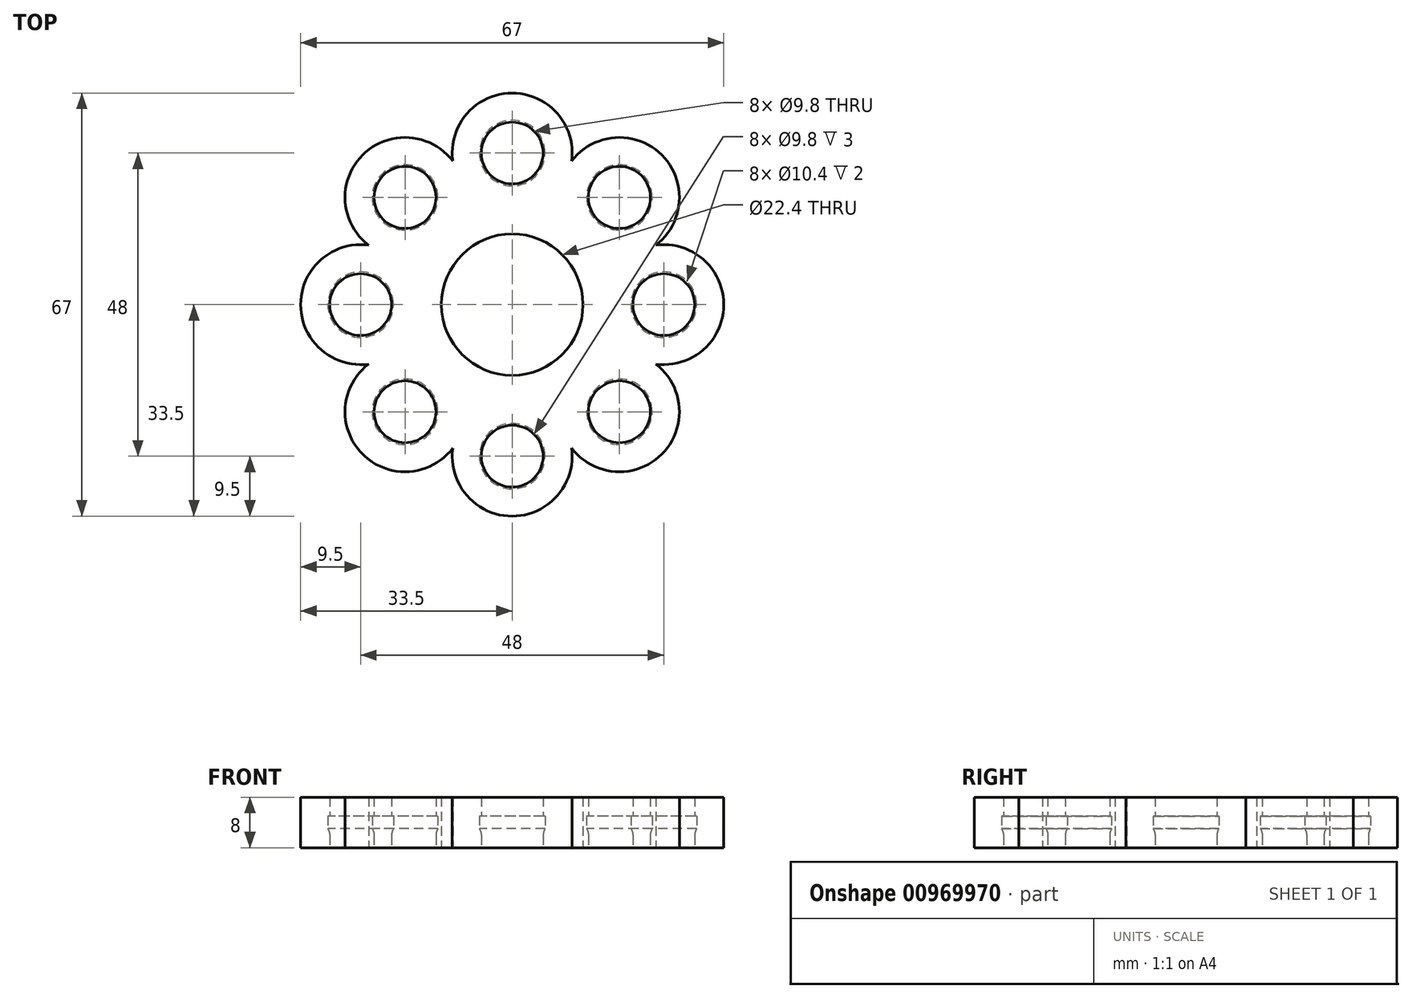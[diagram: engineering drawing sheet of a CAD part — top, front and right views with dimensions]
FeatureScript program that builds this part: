
annotation { "Feature Type Name" : "Feature", "Feature Type Description" : "" }
export const myFeature = defineFeature(function(context is Context, id is Id, definition is map)
    precondition{}
    {
        {
            var Q0;
            Q0=qCreatedBy(makeId("Top.planeOp"),FACE);
            var sketch = newSketch(context, id + "F0", { "sketchPlane" : qUnion([Q0])});
            skCircle(sketch, "E0", {"center": v(0, 0) * mm, "radius": 11.2 * mm});
            skCircle(sketch, "E1", {"center": v(0, 0) * mm, "radius": 24 * mm});
            skCircle(sketch, "E2", {"center": v(-24, 0) * mm, "radius": 5.2 * mm});
            skCircle(sketch, "E3", {"center": v(-24, 0) * mm, "radius": 9.5 * mm});
            skCircle(sketch, "E4", {"center": v(-24, 0) * mm, "radius": 4.9 * mm});
            skCircle(sketch, "E5.1.0", {"center": v(-16.97, -16.97) * mm, "radius": 4.9 * mm});
            skCircle(sketch, "E5.1.1", {"center": v(-16.97, -16.97) * mm, "radius": 5.2 * mm});
            skCircle(sketch, "E5.1.2", {"center": v(-16.97, -16.97) * mm, "radius": 9.5 * mm});
            skCircle(sketch, "E5.2.0", {"center": v(0, -24) * mm, "radius": 4.9 * mm});
            skCircle(sketch, "E5.2.1", {"center": v(0, -24) * mm, "radius": 5.2 * mm});
            skCircle(sketch, "E5.2.2", {"center": v(0, -24) * mm, "radius": 9.5 * mm});
            skCircle(sketch, "E5.3.0", {"center": v(16.97, -16.97) * mm, "radius": 4.9 * mm});
            skCircle(sketch, "E5.3.1", {"center": v(16.97, -16.97) * mm, "radius": 5.2 * mm});
            skCircle(sketch, "E5.3.2", {"center": v(16.97, -16.97) * mm, "radius": 9.5 * mm});
            skCircle(sketch, "E5.4.0", {"center": v(24, 0) * mm, "radius": 4.9 * mm});
            skCircle(sketch, "E5.4.1", {"center": v(24, 0) * mm, "radius": 5.2 * mm});
            skCircle(sketch, "E5.4.2", {"center": v(24, 0) * mm, "radius": 9.5 * mm});
            skCircle(sketch, "E5.5.0", {"center": v(16.97, 16.97) * mm, "radius": 4.9 * mm});
            skCircle(sketch, "E5.5.1", {"center": v(16.97, 16.97) * mm, "radius": 5.2 * mm});
            skCircle(sketch, "E5.5.2", {"center": v(16.97, 16.97) * mm, "radius": 9.5 * mm});
            skCircle(sketch, "E5.6.0", {"center": v(0, 24) * mm, "radius": 4.9 * mm});
            skCircle(sketch, "E5.6.1", {"center": v(0, 24) * mm, "radius": 5.2 * mm});
            skCircle(sketch, "E5.6.2", {"center": v(0, 24) * mm, "radius": 9.5 * mm});
            skCircle(sketch, "E5.7.0", {"center": v(-16.97, 16.97) * mm, "radius": 4.9 * mm});
            skCircle(sketch, "E5.7.1", {"center": v(-16.97, 16.97) * mm, "radius": 5.2 * mm});
            skCircle(sketch, "E5.7.2", {"center": v(-16.97, 16.97) * mm, "radius": 9.5 * mm});
            skSolve(sketch);
        }
        {
            var Q0;
            Q0=makeQuery(id+"F0.imprint","IMPRINT",FACE,{"disambiguationData":[TD([[makeQuery(id+"F0.imprint","IMPRINT",EDGE,{"derivedFrom":sQuery(id+"F0.wireOp",EDGE,"E0")}),-1.0]])]});
            var Q1;
            {var subQ0=sQuery(id+"F0.wireOp",EDGE,"E5.6.2");var subQ1=sQuery(id+"F0.wireOp",EDGE,"E1");var subQ2=makeQuery(id+"F0.imprint","INTERSECT",VERTEX,{"disambiguationData":[OD(1.0)],"derivedFrom":[subQ1,subQ0]});Q1=makeQuery(id+"F0.imprint","IMPRINT",FACE,{"disambiguationData":[TD([[makeQuery(id+"F0.imprint","IMPRINT",EDGE,{"disambiguationData":[TD([[subQ2,-1.0]])],"derivedFrom":subQ1}),1.0]])]});}
            var Q2;
            {var subQ1=sQuery(id+"F0.wireOp",EDGE,"E1");var subQ8=sQuery(id+"F0.wireOp",EDGE,"E5.5.2");var subQ9=makeQuery(id+"F0.imprint","INTERSECT",VERTEX,{"disambiguationData":[OD(1.0)],"derivedFrom":[subQ1,subQ8]});Q2=makeQuery(id+"F0.imprint","IMPRINT",FACE,{"disambiguationData":[TD([[makeQuery(id+"F0.imprint","IMPRINT",EDGE,{"disambiguationData":[TD([[subQ9,-1.0]])],"derivedFrom":subQ1}),1.0]])]});}
            var Q3;
            {var subQ1=sQuery(id+"F0.wireOp",EDGE,"E1");var subQ8=sQuery(id+"F0.wireOp",EDGE,"E5.4.2");var subQ9=makeQuery(id+"F0.imprint","INTERSECT",VERTEX,{"disambiguationData":[OD(0.0)],"derivedFrom":[subQ1,subQ8]});Q3=makeQuery(id+"F0.imprint","IMPRINT",FACE,{"disambiguationData":[TD([[makeQuery(id+"F0.imprint","IMPRINT",EDGE,{"disambiguationData":[TD([[subQ9,-1.0]])],"derivedFrom":subQ1}),1.0]])]});}
            var Q4;
            {var subQ1=sQuery(id+"F0.wireOp",EDGE,"E1");var subQ3=sQuery(id+"F0.wireOp",EDGE,"E5.4.1");var subQ5=makeQuery(id+"F0.imprint","INTERSECT",VERTEX,{"disambiguationData":[OD(0.0)],"derivedFrom":[subQ1,subQ3]});Q4=makeQuery(id+"F0.imprint","IMPRINT",FACE,{"disambiguationData":[TD([[makeQuery(id+"F0.imprint","IMPRINT",EDGE,{"disambiguationData":[TD([[subQ5,-1.0]])],"derivedFrom":subQ1}),1.0]])]});}
            var Q5;
            {var subQ1=sQuery(id+"F0.wireOp",EDGE,"E1");var subQ8=sQuery(id+"F0.wireOp",EDGE,"E5.2.2");var subQ9=makeQuery(id+"F0.imprint","INTERSECT",VERTEX,{"disambiguationData":[OD(1.0)],"derivedFrom":[subQ1,subQ8]});Q5=makeQuery(id+"F0.imprint","IMPRINT",FACE,{"disambiguationData":[TD([[makeQuery(id+"F0.imprint","IMPRINT",EDGE,{"disambiguationData":[TD([[subQ9,-1.0]])],"derivedFrom":subQ1}),1.0]])]});}
            var Q6;
            {var subQ1=sQuery(id+"F0.wireOp",EDGE,"E1");var subQ8=sQuery(id+"F0.wireOp",EDGE,"E5.1.2");var subQ9=makeQuery(id+"F0.imprint","INTERSECT",VERTEX,{"disambiguationData":[OD(1.0)],"derivedFrom":[subQ1,subQ8]});Q6=makeQuery(id+"F0.imprint","IMPRINT",FACE,{"disambiguationData":[TD([[makeQuery(id+"F0.imprint","IMPRINT",EDGE,{"disambiguationData":[TD([[subQ9,-1.0]])],"derivedFrom":subQ1}),1.0]])]});}
            var Q7;
            {var subQ0=sQuery(id+"F0.wireOp",EDGE,"E3");var subQ1=sQuery(id+"F0.wireOp",EDGE,"E1");var subQ2=makeQuery(id+"F0.imprint","INTERSECT",VERTEX,{"disambiguationData":[OD(1.0)],"derivedFrom":[subQ1,subQ0]});Q7=makeQuery(id+"F0.imprint","IMPRINT",FACE,{"disambiguationData":[TD([[makeQuery(id+"F0.imprint","IMPRINT",EDGE,{"disambiguationData":[TD([[subQ2,-1.0]])],"derivedFrom":subQ1}),1.0]])]});}
            var Q8;
            {var subQ1=sQuery(id+"F0.wireOp",EDGE,"E1");var subQ4=sQuery(id+"F0.wireOp",EDGE,"E5.7.2");var subQ5=makeQuery(id+"F0.imprint","INTERSECT",VERTEX,{"disambiguationData":[OD(1.0)],"derivedFrom":[subQ1,subQ4]});Q8=makeQuery(id+"F0.imprint","IMPRINT",FACE,{"disambiguationData":[TD([[makeQuery(id+"F0.imprint","IMPRINT",EDGE,{"disambiguationData":[TD([[subQ5,-1.0]])],"derivedFrom":subQ1}),1.0]])]});}
            var Q9;
            {var subQ0=sQuery(id+"F0.wireOp",EDGE,"E5.2.2");var subQ1=sQuery(id+"F0.wireOp",EDGE,"E1");var subQ2=makeQuery(id+"F0.imprint","INTERSECT",VERTEX,{"disambiguationData":[OD(0.0)],"derivedFrom":[subQ1,subQ0]});Q9=makeQuery(id+"F0.imprint","IMPRINT",FACE,{"disambiguationData":[TD([[makeQuery(id+"F0.imprint","IMPRINT",EDGE,{"disambiguationData":[TD([[subQ2,-1.0]])],"derivedFrom":subQ1}),1.0]])]});}
            var Q10;
            {var subQ0=sQuery(id+"F0.wireOp",EDGE,"E5.2.2");var subQ1=sQuery(id+"F0.wireOp",EDGE,"E1");var subQ2=makeQuery(id+"F0.imprint","INTERSECT",VERTEX,{"disambiguationData":[OD(0.0)],"derivedFrom":[subQ1,subQ0]});Q10=makeQuery(id+"F0.imprint","IMPRINT",FACE,{"disambiguationData":[TD([[makeQuery(id+"F0.imprint","IMPRINT",EDGE,{"disambiguationData":[TD([[subQ2,-1.0]])],"derivedFrom":subQ1}),-1.0]])]});}
            var Q11;
            {var subQ0=sQuery(id+"F0.wireOp",EDGE,"E5.1.1");var subQ1=sQuery(id+"F0.wireOp",EDGE,"E1");var subQ2=makeQuery(id+"F0.imprint","INTERSECT",VERTEX,{"disambiguationData":[OD(0.0)],"derivedFrom":[subQ1,subQ0]});Q11=makeQuery(id+"F0.imprint","IMPRINT",FACE,{"disambiguationData":[TD([[makeQuery(id+"F0.imprint","IMPRINT",EDGE,{"disambiguationData":[TD([[subQ2,-1.0]])],"derivedFrom":subQ1}),1.0]])]});}
            var Q12;
            {var subQ0=sQuery(id+"F0.wireOp",EDGE,"E5.1.1");var subQ1=sQuery(id+"F0.wireOp",EDGE,"E1");var subQ2=makeQuery(id+"F0.imprint","INTERSECT",VERTEX,{"disambiguationData":[OD(0.0)],"derivedFrom":[subQ1,subQ0]});Q12=makeQuery(id+"F0.imprint","IMPRINT",FACE,{"disambiguationData":[TD([[makeQuery(id+"F0.imprint","IMPRINT",EDGE,{"disambiguationData":[TD([[subQ2,-1.0]])],"derivedFrom":subQ1}),-1.0]])]});}
            var Q13;
            {var subQ1=sQuery(id+"F0.wireOp",EDGE,"E1");var subQ4=sQuery(id+"F0.wireOp",EDGE,"E3");var subQ5=makeQuery(id+"F0.imprint","INTERSECT",VERTEX,{"disambiguationData":[OD(1.0)],"derivedFrom":[subQ1,subQ4]});Q13=makeQuery(id+"F0.imprint","IMPRINT",FACE,{"disambiguationData":[TD([[makeQuery(id+"F0.imprint","IMPRINT",EDGE,{"disambiguationData":[TD([[subQ5,-1.0]])],"derivedFrom":subQ1}),-1.0]])]});}
            var Q14;
            {var subQ1=sQuery(id+"F0.wireOp",EDGE,"E1");var subQ7=sQuery(id+"F0.wireOp",EDGE,"E5.1.2");var subQ9=makeQuery(id+"F0.imprint","INTERSECT",VERTEX,{"disambiguationData":[OD(1.0)],"derivedFrom":[subQ1,subQ7]});Q14=makeQuery(id+"F0.imprint","IMPRINT",FACE,{"disambiguationData":[TD([[makeQuery(id+"F0.imprint","IMPRINT",EDGE,{"disambiguationData":[TD([[subQ9,-1.0]])],"derivedFrom":subQ1}),-1.0]])]});}
            var Q15;
            {var subQ0=sQuery(id+"F0.wireOp",EDGE,"E5.2.1");var subQ1=sQuery(id+"F0.wireOp",EDGE,"E1");var subQ2=makeQuery(id+"F0.imprint","INTERSECT",VERTEX,{"disambiguationData":[OD(0.0)],"derivedFrom":[subQ1,subQ0]});Q15=makeQuery(id+"F0.imprint","IMPRINT",FACE,{"disambiguationData":[TD([[makeQuery(id+"F0.imprint","IMPRINT",EDGE,{"disambiguationData":[TD([[subQ2,-1.0]])],"derivedFrom":subQ1}),1.0]])]});}
            var Q16;
            {var subQ0=sQuery(id+"F0.wireOp",EDGE,"E5.2.1");var subQ1=sQuery(id+"F0.wireOp",EDGE,"E1");var subQ2=makeQuery(id+"F0.imprint","INTERSECT",VERTEX,{"disambiguationData":[OD(0.0)],"derivedFrom":[subQ1,subQ0]});Q16=makeQuery(id+"F0.imprint","IMPRINT",FACE,{"disambiguationData":[TD([[makeQuery(id+"F0.imprint","IMPRINT",EDGE,{"disambiguationData":[TD([[subQ2,-1.0]])],"derivedFrom":subQ1}),-1.0]])]});}
            var Q17;
            {var subQ0=sQuery(id+"F0.wireOp",EDGE,"E5.3.2");var subQ1=sQuery(id+"F0.wireOp",EDGE,"E1");var subQ2=makeQuery(id+"F0.imprint","INTERSECT",VERTEX,{"disambiguationData":[OD(0.0)],"derivedFrom":[subQ1,subQ0]});Q17=makeQuery(id+"F0.imprint","IMPRINT",FACE,{"disambiguationData":[TD([[makeQuery(id+"F0.imprint","IMPRINT",EDGE,{"disambiguationData":[TD([[subQ2,-1.0]])],"derivedFrom":subQ1}),1.0]])]});}
            var Q18;
            {var subQ0=sQuery(id+"F0.wireOp",EDGE,"E5.3.2");var subQ1=sQuery(id+"F0.wireOp",EDGE,"E1");var subQ2=makeQuery(id+"F0.imprint","INTERSECT",VERTEX,{"disambiguationData":[OD(0.0)],"derivedFrom":[subQ1,subQ0]});Q18=makeQuery(id+"F0.imprint","IMPRINT",FACE,{"disambiguationData":[TD([[makeQuery(id+"F0.imprint","IMPRINT",EDGE,{"disambiguationData":[TD([[subQ2,-1.0]])],"derivedFrom":subQ1}),-1.0]])]});}
            var Q19;
            {var subQ1=sQuery(id+"F0.wireOp",EDGE,"E1");var subQ5=sQuery(id+"F0.wireOp",EDGE,"E5.2.2");var subQ7=makeQuery(id+"F0.imprint","INTERSECT",VERTEX,{"disambiguationData":[OD(1.0)],"derivedFrom":[subQ1,subQ5]});Q19=makeQuery(id+"F0.imprint","IMPRINT",FACE,{"disambiguationData":[TD([[makeQuery(id+"F0.imprint","IMPRINT",EDGE,{"disambiguationData":[TD([[subQ7,-1.0]])],"derivedFrom":subQ1}),-1.0]])]});}
            var Q20;
            {var subQ0=sQuery(id+"F0.wireOp",EDGE,"E5.3.1");var subQ1=sQuery(id+"F0.wireOp",EDGE,"E1");var subQ2=makeQuery(id+"F0.imprint","INTERSECT",VERTEX,{"disambiguationData":[OD(0.0)],"derivedFrom":[subQ1,subQ0]});Q20=makeQuery(id+"F0.imprint","IMPRINT",FACE,{"disambiguationData":[TD([[makeQuery(id+"F0.imprint","IMPRINT",EDGE,{"disambiguationData":[TD([[subQ2,-1.0]])],"derivedFrom":subQ1}),-1.0]])]});}
            var Q21;
            {var subQ0=sQuery(id+"F0.wireOp",EDGE,"E5.3.1");var subQ1=sQuery(id+"F0.wireOp",EDGE,"E1");var subQ2=makeQuery(id+"F0.imprint","INTERSECT",VERTEX,{"disambiguationData":[OD(0.0)],"derivedFrom":[subQ1,subQ0]});Q21=makeQuery(id+"F0.imprint","IMPRINT",FACE,{"disambiguationData":[TD([[makeQuery(id+"F0.imprint","IMPRINT",EDGE,{"disambiguationData":[TD([[subQ2,-1.0]])],"derivedFrom":subQ1}),1.0]])]});}
            var Q22;
            {var subQ0=sQuery(id+"F0.wireOp",EDGE,"E5.4.2");var subQ1=sQuery(id+"F0.wireOp",EDGE,"E1");var subQ2=makeQuery(id+"F0.imprint","INTERSECT",VERTEX,{"disambiguationData":[OD(1.0)],"derivedFrom":[subQ1,subQ0]});Q22=makeQuery(id+"F0.imprint","IMPRINT",FACE,{"disambiguationData":[TD([[makeQuery(id+"F0.imprint","IMPRINT",EDGE,{"disambiguationData":[TD([[subQ2,-1.0]])],"derivedFrom":subQ1}),1.0]])]});}
            var Q23;
            {var subQ0=sQuery(id+"F0.wireOp",EDGE,"E5.4.2");var subQ1=sQuery(id+"F0.wireOp",EDGE,"E1");var subQ2=makeQuery(id+"F0.imprint","INTERSECT",VERTEX,{"disambiguationData":[OD(1.0)],"derivedFrom":[subQ1,subQ0]});Q23=makeQuery(id+"F0.imprint","IMPRINT",FACE,{"disambiguationData":[TD([[makeQuery(id+"F0.imprint","IMPRINT",EDGE,{"disambiguationData":[TD([[subQ2,-1.0]])],"derivedFrom":subQ1}),-1.0]])]});}
            var Q24;
            {var subQ0=sQuery(id+"F0.wireOp",EDGE,"E5.4.1");var subQ1=sQuery(id+"F0.wireOp",EDGE,"E1");var subQ2=makeQuery(id+"F0.imprint","INTERSECT",VERTEX,{"disambiguationData":[OD(0.0)],"derivedFrom":[subQ1,subQ0]});Q24=makeQuery(id+"F0.imprint","IMPRINT",FACE,{"disambiguationData":[TD([[makeQuery(id+"F0.imprint","IMPRINT",EDGE,{"disambiguationData":[TD([[subQ2,-1.0]])],"derivedFrom":subQ1}),-1.0]])]});}
            var Q25;
            {var subQ0=sQuery(id+"F0.wireOp",EDGE,"E5.4.1");var subQ1=sQuery(id+"F0.wireOp",EDGE,"E1");var subQ2=makeQuery(id+"F0.imprint","INTERSECT",VERTEX,{"disambiguationData":[OD(0.0)],"derivedFrom":[subQ1,subQ0]});Q25=makeQuery(id+"F0.imprint","IMPRINT",FACE,{"disambiguationData":[TD([[makeQuery(id+"F0.imprint","IMPRINT",EDGE,{"disambiguationData":[TD([[subQ2,1.0]])],"derivedFrom":subQ1}),-1.0]])]});}
            var Q26;
            {var subQ0=sQuery(id+"F0.wireOp",EDGE,"E5.4.1");var subQ1=sQuery(id+"F0.wireOp",EDGE,"E1");var subQ2=makeQuery(id+"F0.imprint","INTERSECT",VERTEX,{"disambiguationData":[OD(0.0)],"derivedFrom":[subQ1,subQ0]});Q26=makeQuery(id+"F0.imprint","IMPRINT",FACE,{"disambiguationData":[TD([[makeQuery(id+"F0.imprint","IMPRINT",EDGE,{"disambiguationData":[TD([[subQ2,1.0]])],"derivedFrom":subQ1}),1.0]])]});}
            var Q27;
            {var subQ0=sQuery(id+"F0.wireOp",EDGE,"E5.5.2");var subQ1=sQuery(id+"F0.wireOp",EDGE,"E1");var subQ2=makeQuery(id+"F0.imprint","INTERSECT",VERTEX,{"disambiguationData":[OD(0.0)],"derivedFrom":[subQ1,subQ0]});Q27=makeQuery(id+"F0.imprint","IMPRINT",FACE,{"disambiguationData":[TD([[makeQuery(id+"F0.imprint","IMPRINT",EDGE,{"disambiguationData":[TD([[subQ2,-1.0]])],"derivedFrom":subQ1}),1.0]])]});}
            var Q28;
            {var subQ0=sQuery(id+"F0.wireOp",EDGE,"E5.5.2");var subQ1=sQuery(id+"F0.wireOp",EDGE,"E1");var subQ2=makeQuery(id+"F0.imprint","INTERSECT",VERTEX,{"disambiguationData":[OD(0.0)],"derivedFrom":[subQ1,subQ0]});Q28=makeQuery(id+"F0.imprint","IMPRINT",FACE,{"disambiguationData":[TD([[makeQuery(id+"F0.imprint","IMPRINT",EDGE,{"disambiguationData":[TD([[subQ2,-1.0]])],"derivedFrom":subQ1}),-1.0]])]});}
            var Q29;
            {var subQ1=sQuery(id+"F0.wireOp",EDGE,"E1");var subQ5=sQuery(id+"F0.wireOp",EDGE,"E5.4.2");var subQ7=makeQuery(id+"F0.imprint","INTERSECT",VERTEX,{"disambiguationData":[OD(0.0)],"derivedFrom":[subQ1,subQ5]});Q29=makeQuery(id+"F0.imprint","IMPRINT",FACE,{"disambiguationData":[TD([[makeQuery(id+"F0.imprint","IMPRINT",EDGE,{"disambiguationData":[TD([[subQ7,-1.0]])],"derivedFrom":subQ1}),-1.0]])]});}
            var Q30;
            {var subQ0=sQuery(id+"F0.wireOp",EDGE,"E5.5.1");var subQ1=sQuery(id+"F0.wireOp",EDGE,"E1");var subQ2=makeQuery(id+"F0.imprint","INTERSECT",VERTEX,{"disambiguationData":[OD(0.0)],"derivedFrom":[subQ1,subQ0]});Q30=makeQuery(id+"F0.imprint","IMPRINT",FACE,{"disambiguationData":[TD([[makeQuery(id+"F0.imprint","IMPRINT",EDGE,{"disambiguationData":[TD([[subQ2,-1.0]])],"derivedFrom":subQ1}),-1.0]])]});}
            var Q31;
            {var subQ0=sQuery(id+"F0.wireOp",EDGE,"E5.5.1");var subQ1=sQuery(id+"F0.wireOp",EDGE,"E1");var subQ2=makeQuery(id+"F0.imprint","INTERSECT",VERTEX,{"disambiguationData":[OD(0.0)],"derivedFrom":[subQ1,subQ0]});Q31=makeQuery(id+"F0.imprint","IMPRINT",FACE,{"disambiguationData":[TD([[makeQuery(id+"F0.imprint","IMPRINT",EDGE,{"disambiguationData":[TD([[subQ2,-1.0]])],"derivedFrom":subQ1}),1.0]])]});}
            var Q32;
            {var subQ0=sQuery(id+"F0.wireOp",EDGE,"E5.6.2");var subQ1=sQuery(id+"F0.wireOp",EDGE,"E1");var subQ2=makeQuery(id+"F0.imprint","INTERSECT",VERTEX,{"disambiguationData":[OD(0.0)],"derivedFrom":[subQ1,subQ0]});Q32=makeQuery(id+"F0.imprint","IMPRINT",FACE,{"disambiguationData":[TD([[makeQuery(id+"F0.imprint","IMPRINT",EDGE,{"disambiguationData":[TD([[subQ2,-1.0]])],"derivedFrom":subQ1}),1.0]])]});}
            var Q33;
            {var subQ0=sQuery(id+"F0.wireOp",EDGE,"E5.6.2");var subQ1=sQuery(id+"F0.wireOp",EDGE,"E1");var subQ2=makeQuery(id+"F0.imprint","INTERSECT",VERTEX,{"disambiguationData":[OD(0.0)],"derivedFrom":[subQ1,subQ0]});Q33=makeQuery(id+"F0.imprint","IMPRINT",FACE,{"disambiguationData":[TD([[makeQuery(id+"F0.imprint","IMPRINT",EDGE,{"disambiguationData":[TD([[subQ2,-1.0]])],"derivedFrom":subQ1}),-1.0]])]});}
            var Q34;
            {var subQ1=sQuery(id+"F0.wireOp",EDGE,"E1");var subQ5=sQuery(id+"F0.wireOp",EDGE,"E5.5.2");var subQ7=makeQuery(id+"F0.imprint","INTERSECT",VERTEX,{"disambiguationData":[OD(1.0)],"derivedFrom":[subQ1,subQ5]});Q34=makeQuery(id+"F0.imprint","IMPRINT",FACE,{"disambiguationData":[TD([[makeQuery(id+"F0.imprint","IMPRINT",EDGE,{"disambiguationData":[TD([[subQ7,-1.0]])],"derivedFrom":subQ1}),-1.0]])]});}
            var Q35;
            {var subQ0=sQuery(id+"F0.wireOp",EDGE,"E5.6.1");var subQ1=sQuery(id+"F0.wireOp",EDGE,"E1");var subQ2=makeQuery(id+"F0.imprint","INTERSECT",VERTEX,{"disambiguationData":[OD(0.0)],"derivedFrom":[subQ1,subQ0]});Q35=makeQuery(id+"F0.imprint","IMPRINT",FACE,{"disambiguationData":[TD([[makeQuery(id+"F0.imprint","IMPRINT",EDGE,{"disambiguationData":[TD([[subQ2,-1.0]])],"derivedFrom":subQ1}),-1.0]])]});}
            var Q36;
            {var subQ0=sQuery(id+"F0.wireOp",EDGE,"E5.6.1");var subQ1=sQuery(id+"F0.wireOp",EDGE,"E1");var subQ2=makeQuery(id+"F0.imprint","INTERSECT",VERTEX,{"disambiguationData":[OD(0.0)],"derivedFrom":[subQ1,subQ0]});Q36=makeQuery(id+"F0.imprint","IMPRINT",FACE,{"disambiguationData":[TD([[makeQuery(id+"F0.imprint","IMPRINT",EDGE,{"disambiguationData":[TD([[subQ2,-1.0]])],"derivedFrom":subQ1}),1.0]])]});}
            var Q37;
            {var subQ0=sQuery(id+"F0.wireOp",EDGE,"E5.7.2");var subQ1=sQuery(id+"F0.wireOp",EDGE,"E1");var subQ2=makeQuery(id+"F0.imprint","INTERSECT",VERTEX,{"disambiguationData":[OD(0.0)],"derivedFrom":[subQ1,subQ0]});Q37=makeQuery(id+"F0.imprint","IMPRINT",FACE,{"disambiguationData":[TD([[makeQuery(id+"F0.imprint","IMPRINT",EDGE,{"disambiguationData":[TD([[subQ2,-1.0]])],"derivedFrom":subQ1}),1.0]])]});}
            var Q38;
            {var subQ0=sQuery(id+"F0.wireOp",EDGE,"E5.7.2");var subQ1=sQuery(id+"F0.wireOp",EDGE,"E1");var subQ2=makeQuery(id+"F0.imprint","INTERSECT",VERTEX,{"disambiguationData":[OD(0.0)],"derivedFrom":[subQ1,subQ0]});Q38=makeQuery(id+"F0.imprint","IMPRINT",FACE,{"disambiguationData":[TD([[makeQuery(id+"F0.imprint","IMPRINT",EDGE,{"disambiguationData":[TD([[subQ2,-1.0]])],"derivedFrom":subQ1}),-1.0]])]});}
            var Q39;
            {var subQ3=sQuery(id+"F0.wireOp",EDGE,"E1");var subQ7=sQuery(id+"F0.wireOp",EDGE,"E5.6.2");var subQ9=makeQuery(id+"F0.imprint","INTERSECT",VERTEX,{"disambiguationData":[OD(1.0)],"derivedFrom":[subQ3,subQ7]});Q39=makeQuery(id+"F0.imprint","IMPRINT",FACE,{"disambiguationData":[TD([[makeQuery(id+"F0.imprint","IMPRINT",EDGE,{"disambiguationData":[TD([[subQ9,-1.0]])],"derivedFrom":subQ3}),-1.0]])]});}
            var Q40;
            {var subQ0=sQuery(id+"F0.wireOp",EDGE,"E5.7.1");var subQ1=sQuery(id+"F0.wireOp",EDGE,"E1");var subQ2=makeQuery(id+"F0.imprint","INTERSECT",VERTEX,{"disambiguationData":[OD(0.0)],"derivedFrom":[subQ1,subQ0]});Q40=makeQuery(id+"F0.imprint","IMPRINT",FACE,{"disambiguationData":[TD([[makeQuery(id+"F0.imprint","IMPRINT",EDGE,{"disambiguationData":[TD([[subQ2,-1.0]])],"derivedFrom":subQ1}),-1.0]])]});}
            var Q41;
            {var subQ0=sQuery(id+"F0.wireOp",EDGE,"E5.7.1");var subQ1=sQuery(id+"F0.wireOp",EDGE,"E1");var subQ2=makeQuery(id+"F0.imprint","INTERSECT",VERTEX,{"disambiguationData":[OD(0.0)],"derivedFrom":[subQ1,subQ0]});Q41=makeQuery(id+"F0.imprint","IMPRINT",FACE,{"disambiguationData":[TD([[makeQuery(id+"F0.imprint","IMPRINT",EDGE,{"disambiguationData":[TD([[subQ2,-1.0]])],"derivedFrom":subQ1}),1.0]])]});}
            var Q42;
            {var subQ0=sQuery(id+"F0.wireOp",EDGE,"E3");var subQ1=sQuery(id+"F0.wireOp",EDGE,"E1");var subQ2=makeQuery(id+"F0.imprint","INTERSECT",VERTEX,{"disambiguationData":[OD(0.0)],"derivedFrom":[subQ1,subQ0]});Q42=makeQuery(id+"F0.imprint","IMPRINT",FACE,{"disambiguationData":[TD([[makeQuery(id+"F0.imprint","IMPRINT",EDGE,{"disambiguationData":[TD([[subQ2,-1.0]])],"derivedFrom":subQ1}),1.0]])]});}
            var Q43;
            {var subQ0=sQuery(id+"F0.wireOp",EDGE,"E3");var subQ1=sQuery(id+"F0.wireOp",EDGE,"E1");var subQ2=makeQuery(id+"F0.imprint","INTERSECT",VERTEX,{"disambiguationData":[OD(0.0)],"derivedFrom":[subQ1,subQ0]});Q43=makeQuery(id+"F0.imprint","IMPRINT",FACE,{"disambiguationData":[TD([[makeQuery(id+"F0.imprint","IMPRINT",EDGE,{"disambiguationData":[TD([[subQ2,-1.0]])],"derivedFrom":subQ1}),-1.0]])]});}
            var Q44;
            {var subQ0=sQuery(id+"F0.wireOp",EDGE,"E2");var subQ1=sQuery(id+"F0.wireOp",EDGE,"E1");var subQ2=makeQuery(id+"F0.imprint","INTERSECT",VERTEX,{"disambiguationData":[OD(0.0)],"derivedFrom":[subQ1,subQ0]});Q44=makeQuery(id+"F0.imprint","IMPRINT",FACE,{"disambiguationData":[TD([[makeQuery(id+"F0.imprint","IMPRINT",EDGE,{"disambiguationData":[TD([[subQ2,-1.0]])],"derivedFrom":subQ1}),1.0]])]});}
            var Q45;
            {var subQ0=sQuery(id+"F0.wireOp",EDGE,"E5.1.2");var subQ1=sQuery(id+"F0.wireOp",EDGE,"E1");var subQ2=makeQuery(id+"F0.imprint","INTERSECT",VERTEX,{"disambiguationData":[OD(0.0)],"derivedFrom":[subQ1,subQ0]});Q45=makeQuery(id+"F0.imprint","IMPRINT",FACE,{"disambiguationData":[TD([[makeQuery(id+"F0.imprint","IMPRINT",EDGE,{"disambiguationData":[TD([[subQ2,-1.0]])],"derivedFrom":subQ1}),1.0]])]});}
            var Q46;
            {var subQ0=sQuery(id+"F0.wireOp",EDGE,"E5.1.2");var subQ1=sQuery(id+"F0.wireOp",EDGE,"E1");var subQ2=makeQuery(id+"F0.imprint","INTERSECT",VERTEX,{"disambiguationData":[OD(0.0)],"derivedFrom":[subQ1,subQ0]});Q46=makeQuery(id+"F0.imprint","IMPRINT",FACE,{"disambiguationData":[TD([[makeQuery(id+"F0.imprint","IMPRINT",EDGE,{"disambiguationData":[TD([[subQ2,-1.0]])],"derivedFrom":subQ1}),-1.0]])]});}
            var Q47;
            {var subQ0=sQuery(id+"F0.wireOp",EDGE,"E2");var subQ1=sQuery(id+"F0.wireOp",EDGE,"E1");var subQ2=makeQuery(id+"F0.imprint","INTERSECT",VERTEX,{"disambiguationData":[OD(0.0)],"derivedFrom":[subQ1,subQ0]});Q47=makeQuery(id+"F0.imprint","IMPRINT",FACE,{"disambiguationData":[TD([[makeQuery(id+"F0.imprint","IMPRINT",EDGE,{"disambiguationData":[TD([[subQ2,-1.0]])],"derivedFrom":subQ1}),-1.0]])]});}
            var Q48;
            {var subQ0=sQuery(id+"F0.wireOp",EDGE,"E5.7.2");var subQ5=sQuery(id+"F0.wireOp",EDGE,"E1");var subQ10=makeQuery(id+"F0.imprint","INTERSECT",VERTEX,{"disambiguationData":[OD(1.0)],"derivedFrom":[subQ5,subQ0]});Q48=makeQuery(id+"F0.imprint","IMPRINT",FACE,{"disambiguationData":[TD([[makeQuery(id+"F0.imprint","IMPRINT",EDGE,{"disambiguationData":[TD([[subQ10,-1.0]])],"derivedFrom":subQ5}),-1.0]])]});}
            extrude(context, id + "F1", {"entities" : qUnion([Q0, Q1, Q2, Q3, Q4, Q5, Q6, Q7, Q8, Q9, Q10, Q11, Q12, Q13, Q14, Q15, Q16, Q17, Q18, Q19, Q20, Q21, Q22, Q23, Q24, Q25, Q26, Q27, Q28, Q29, Q30, Q31, Q32, Q33, Q34, Q35, Q36, Q37, Q38, Q39, Q40, Q41, Q42, Q43, Q44, Q45, Q46, Q47, Q48]), "depth" : 4 * mm, "offsetDistance" : 25 * mm, "hasSecondDirection" : true, "secondDirectionOppositeDirection" : true, "secondDirectionDepth" : 4 * mm});
        }
        {
            var Q0;
            {var subQ0=sQuery(id+"F0.wireOp",EDGE,"E5.7.1");var subQ1=sQuery(id+"F0.wireOp",EDGE,"E1");var subQ2=makeQuery(id+"F0.imprint","INTERSECT",VERTEX,{"disambiguationData":[OD(0.0)],"derivedFrom":[subQ1,subQ0]});Q0=makeQuery(id+"F0.imprint","IMPRINT",FACE,{"disambiguationData":[TD([[makeQuery(id+"F0.imprint","IMPRINT",EDGE,{"disambiguationData":[TD([[subQ2,-1.0]])],"derivedFrom":subQ1}),1.0]])]});}
            var Q1;
            {var subQ0=sQuery(id+"F0.wireOp",EDGE,"E5.7.1");var subQ1=sQuery(id+"F0.wireOp",EDGE,"E1");var subQ2=makeQuery(id+"F0.imprint","INTERSECT",VERTEX,{"disambiguationData":[OD(0.0)],"derivedFrom":[subQ1,subQ0]});Q1=makeQuery(id+"F0.imprint","IMPRINT",FACE,{"disambiguationData":[TD([[makeQuery(id+"F0.imprint","IMPRINT",EDGE,{"disambiguationData":[TD([[subQ2,-1.0]])],"derivedFrom":subQ1}),-1.0]])]});}
            var Q2;
            {var subQ0=sQuery(id+"F0.wireOp",EDGE,"E2");var subQ1=sQuery(id+"F0.wireOp",EDGE,"E1");var subQ2=makeQuery(id+"F0.imprint","INTERSECT",VERTEX,{"disambiguationData":[OD(0.0)],"derivedFrom":[subQ1,subQ0]});Q2=makeQuery(id+"F0.imprint","IMPRINT",FACE,{"disambiguationData":[TD([[makeQuery(id+"F0.imprint","IMPRINT",EDGE,{"disambiguationData":[TD([[subQ2,-1.0]])],"derivedFrom":subQ1}),1.0]])]});}
            var Q3;
            {var subQ0=sQuery(id+"F0.wireOp",EDGE,"E2");var subQ1=sQuery(id+"F0.wireOp",EDGE,"E1");var subQ2=makeQuery(id+"F0.imprint","INTERSECT",VERTEX,{"disambiguationData":[OD(0.0)],"derivedFrom":[subQ1,subQ0]});Q3=makeQuery(id+"F0.imprint","IMPRINT",FACE,{"disambiguationData":[TD([[makeQuery(id+"F0.imprint","IMPRINT",EDGE,{"disambiguationData":[TD([[subQ2,-1.0]])],"derivedFrom":subQ1}),-1.0]])]});}
            var Q4;
            {var subQ0=sQuery(id+"F0.wireOp",EDGE,"E5.1.1");var subQ1=sQuery(id+"F0.wireOp",EDGE,"E1");var subQ2=makeQuery(id+"F0.imprint","INTERSECT",VERTEX,{"disambiguationData":[OD(0.0)],"derivedFrom":[subQ1,subQ0]});Q4=makeQuery(id+"F0.imprint","IMPRINT",FACE,{"disambiguationData":[TD([[makeQuery(id+"F0.imprint","IMPRINT",EDGE,{"disambiguationData":[TD([[subQ2,-1.0]])],"derivedFrom":subQ1}),1.0]])]});}
            var Q5;
            {var subQ0=sQuery(id+"F0.wireOp",EDGE,"E5.1.1");var subQ1=sQuery(id+"F0.wireOp",EDGE,"E1");var subQ2=makeQuery(id+"F0.imprint","INTERSECT",VERTEX,{"disambiguationData":[OD(0.0)],"derivedFrom":[subQ1,subQ0]});Q5=makeQuery(id+"F0.imprint","IMPRINT",FACE,{"disambiguationData":[TD([[makeQuery(id+"F0.imprint","IMPRINT",EDGE,{"disambiguationData":[TD([[subQ2,-1.0]])],"derivedFrom":subQ1}),-1.0]])]});}
            var Q6;
            {var subQ0=sQuery(id+"F0.wireOp",EDGE,"E5.2.1");var subQ1=sQuery(id+"F0.wireOp",EDGE,"E1");var subQ2=makeQuery(id+"F0.imprint","INTERSECT",VERTEX,{"disambiguationData":[OD(0.0)],"derivedFrom":[subQ1,subQ0]});Q6=makeQuery(id+"F0.imprint","IMPRINT",FACE,{"disambiguationData":[TD([[makeQuery(id+"F0.imprint","IMPRINT",EDGE,{"disambiguationData":[TD([[subQ2,-1.0]])],"derivedFrom":subQ1}),1.0]])]});}
            var Q7;
            {var subQ0=sQuery(id+"F0.wireOp",EDGE,"E5.2.1");var subQ1=sQuery(id+"F0.wireOp",EDGE,"E1");var subQ2=makeQuery(id+"F0.imprint","INTERSECT",VERTEX,{"disambiguationData":[OD(0.0)],"derivedFrom":[subQ1,subQ0]});Q7=makeQuery(id+"F0.imprint","IMPRINT",FACE,{"disambiguationData":[TD([[makeQuery(id+"F0.imprint","IMPRINT",EDGE,{"disambiguationData":[TD([[subQ2,-1.0]])],"derivedFrom":subQ1}),-1.0]])]});}
            var Q8;
            {var subQ0=sQuery(id+"F0.wireOp",EDGE,"E5.3.1");var subQ1=sQuery(id+"F0.wireOp",EDGE,"E1");var subQ2=makeQuery(id+"F0.imprint","INTERSECT",VERTEX,{"disambiguationData":[OD(0.0)],"derivedFrom":[subQ1,subQ0]});Q8=makeQuery(id+"F0.imprint","IMPRINT",FACE,{"disambiguationData":[TD([[makeQuery(id+"F0.imprint","IMPRINT",EDGE,{"disambiguationData":[TD([[subQ2,-1.0]])],"derivedFrom":subQ1}),1.0]])]});}
            var Q9;
            {var subQ0=sQuery(id+"F0.wireOp",EDGE,"E5.3.1");var subQ1=sQuery(id+"F0.wireOp",EDGE,"E1");var subQ2=makeQuery(id+"F0.imprint","INTERSECT",VERTEX,{"disambiguationData":[OD(0.0)],"derivedFrom":[subQ1,subQ0]});Q9=makeQuery(id+"F0.imprint","IMPRINT",FACE,{"disambiguationData":[TD([[makeQuery(id+"F0.imprint","IMPRINT",EDGE,{"disambiguationData":[TD([[subQ2,-1.0]])],"derivedFrom":subQ1}),-1.0]])]});}
            var Q10;
            {var subQ0=sQuery(id+"F0.wireOp",EDGE,"E5.4.1");var subQ1=sQuery(id+"F0.wireOp",EDGE,"E1");var subQ2=makeQuery(id+"F0.imprint","INTERSECT",VERTEX,{"disambiguationData":[OD(0.0)],"derivedFrom":[subQ1,subQ0]});Q10=makeQuery(id+"F0.imprint","IMPRINT",FACE,{"disambiguationData":[TD([[makeQuery(id+"F0.imprint","IMPRINT",EDGE,{"disambiguationData":[TD([[subQ2,1.0]])],"derivedFrom":subQ1}),-1.0]])]});}
            var Q11;
            {var subQ0=sQuery(id+"F0.wireOp",EDGE,"E5.4.1");var subQ1=sQuery(id+"F0.wireOp",EDGE,"E1");var subQ2=makeQuery(id+"F0.imprint","INTERSECT",VERTEX,{"disambiguationData":[OD(0.0)],"derivedFrom":[subQ1,subQ0]});Q11=makeQuery(id+"F0.imprint","IMPRINT",FACE,{"disambiguationData":[TD([[makeQuery(id+"F0.imprint","IMPRINT",EDGE,{"disambiguationData":[TD([[subQ2,1.0]])],"derivedFrom":subQ1}),1.0]])]});}
            var Q12;
            {var subQ0=sQuery(id+"F0.wireOp",EDGE,"E5.5.1");var subQ1=sQuery(id+"F0.wireOp",EDGE,"E1");var subQ2=makeQuery(id+"F0.imprint","INTERSECT",VERTEX,{"disambiguationData":[OD(0.0)],"derivedFrom":[subQ1,subQ0]});Q12=makeQuery(id+"F0.imprint","IMPRINT",FACE,{"disambiguationData":[TD([[makeQuery(id+"F0.imprint","IMPRINT",EDGE,{"disambiguationData":[TD([[subQ2,-1.0]])],"derivedFrom":subQ1}),1.0]])]});}
            var Q13;
            {var subQ0=sQuery(id+"F0.wireOp",EDGE,"E5.5.1");var subQ1=sQuery(id+"F0.wireOp",EDGE,"E1");var subQ2=makeQuery(id+"F0.imprint","INTERSECT",VERTEX,{"disambiguationData":[OD(0.0)],"derivedFrom":[subQ1,subQ0]});Q13=makeQuery(id+"F0.imprint","IMPRINT",FACE,{"disambiguationData":[TD([[makeQuery(id+"F0.imprint","IMPRINT",EDGE,{"disambiguationData":[TD([[subQ2,-1.0]])],"derivedFrom":subQ1}),-1.0]])]});}
            var Q14;
            {var subQ0=sQuery(id+"F0.wireOp",EDGE,"E5.6.1");var subQ1=sQuery(id+"F0.wireOp",EDGE,"E1");var subQ2=makeQuery(id+"F0.imprint","INTERSECT",VERTEX,{"disambiguationData":[OD(0.0)],"derivedFrom":[subQ1,subQ0]});Q14=makeQuery(id+"F0.imprint","IMPRINT",FACE,{"disambiguationData":[TD([[makeQuery(id+"F0.imprint","IMPRINT",EDGE,{"disambiguationData":[TD([[subQ2,-1.0]])],"derivedFrom":subQ1}),-1.0]])]});}
            var Q15;
            {var subQ0=sQuery(id+"F0.wireOp",EDGE,"E5.6.1");var subQ1=sQuery(id+"F0.wireOp",EDGE,"E1");var subQ2=makeQuery(id+"F0.imprint","INTERSECT",VERTEX,{"disambiguationData":[OD(0.0)],"derivedFrom":[subQ1,subQ0]});Q15=makeQuery(id+"F0.imprint","IMPRINT",FACE,{"disambiguationData":[TD([[makeQuery(id+"F0.imprint","IMPRINT",EDGE,{"disambiguationData":[TD([[subQ2,-1.0]])],"derivedFrom":subQ1}),1.0]])]});}
            extrude(context, id + "F2", {"entities" : qUnion([Q0, Q1, Q2, Q3, Q4, Q5, Q6, Q7, Q8, Q9, Q10, Q11, Q12, Q13, Q14, Q15]), "operationType" : NewBodyOperationType.REMOVE, "depth" : 1 * mm, "offsetDistance" : 25 * mm, "hasSecondDirection" : true, "secondDirectionOppositeDirection" : true, "secondDirectionDepth" : 1 * mm});
        }
        {
            var Q0;
            Q0=makeQuery(id+"F2.boolean.opBoolean","COPY",EDGE,{"derivedFrom":makeQuery(id+"F2.opExtrude","CAP_EDGE",EDGE,{"disambiguationData":[OSD([sQuery(id+"F0.wireOp",EDGE,"E5.7.0")])],"isStart":true})});
            var Q1;
            Q1=makeQuery(id+"F2.boolean.opBoolean","COPY",EDGE,{"derivedFrom":makeQuery(id+"F2.opExtrude","CAP_EDGE",EDGE,{"disambiguationData":[OSD([sQuery(id+"F0.wireOp",EDGE,"E5.7.0")])],"isStart":false})});
            var Q2;
            Q2=makeQuery(id+"F2.boolean.opBoolean","COPY",EDGE,{"derivedFrom":makeQuery(id+"F2.opExtrude","CAP_EDGE",EDGE,{"disambiguationData":[OSD([sQuery(id+"F0.wireOp",EDGE,"E5.6.0")])],"isStart":true})});
            var Q3;
            Q3=makeQuery(id+"F2.boolean.opBoolean","COPY",EDGE,{"derivedFrom":makeQuery(id+"F2.opExtrude","CAP_EDGE",EDGE,{"disambiguationData":[OSD([sQuery(id+"F0.wireOp",EDGE,"E5.6.0")])],"isStart":false})});
            var Q4;
            Q4=makeQuery(id+"F2.boolean.opBoolean","COPY",EDGE,{"derivedFrom":makeQuery(id+"F2.opExtrude","CAP_EDGE",EDGE,{"disambiguationData":[OSD([sQuery(id+"F0.wireOp",EDGE,"E5.5.0")])],"isStart":true})});
            var Q5;
            Q5=makeQuery(id+"F2.boolean.opBoolean","COPY",EDGE,{"derivedFrom":makeQuery(id+"F2.opExtrude","CAP_EDGE",EDGE,{"disambiguationData":[OSD([sQuery(id+"F0.wireOp",EDGE,"E5.5.0")])],"isStart":false})});
            var Q6;
            Q6=makeQuery(id+"F2.boolean.opBoolean","COPY",EDGE,{"derivedFrom":makeQuery(id+"F2.opExtrude","CAP_EDGE",EDGE,{"disambiguationData":[OSD([sQuery(id+"F0.wireOp",EDGE,"E4")])],"isStart":true})});
            var Q7;
            Q7=makeQuery(id+"F2.boolean.opBoolean","COPY",EDGE,{"derivedFrom":makeQuery(id+"F2.opExtrude","CAP_EDGE",EDGE,{"disambiguationData":[OSD([sQuery(id+"F0.wireOp",EDGE,"E4")])],"isStart":false})});
            var Q8;
            Q8=makeQuery(id+"F2.boolean.opBoolean","COPY",EDGE,{"derivedFrom":makeQuery(id+"F2.opExtrude","CAP_EDGE",EDGE,{"disambiguationData":[OSD([sQuery(id+"F0.wireOp",EDGE,"E5.4.0")])],"isStart":true})});
            var Q9;
            Q9=makeQuery(id+"F2.boolean.opBoolean","COPY",EDGE,{"derivedFrom":makeQuery(id+"F2.opExtrude","CAP_EDGE",EDGE,{"disambiguationData":[OSD([sQuery(id+"F0.wireOp",EDGE,"E5.4.0")])],"isStart":false})});
            var Q10;
            Q10=makeQuery(id+"F2.boolean.opBoolean","COPY",EDGE,{"derivedFrom":makeQuery(id+"F2.opExtrude","CAP_EDGE",EDGE,{"disambiguationData":[OSD([sQuery(id+"F0.wireOp",EDGE,"E5.3.0")])],"isStart":true})});
            var Q11;
            Q11=makeQuery(id+"F2.boolean.opBoolean","COPY",EDGE,{"derivedFrom":makeQuery(id+"F2.opExtrude","CAP_EDGE",EDGE,{"disambiguationData":[OSD([sQuery(id+"F0.wireOp",EDGE,"E5.3.0")])],"isStart":false})});
            var Q12;
            Q12=makeQuery(id+"F2.boolean.opBoolean","COPY",EDGE,{"derivedFrom":makeQuery(id+"F2.opExtrude","CAP_EDGE",EDGE,{"disambiguationData":[OSD([sQuery(id+"F0.wireOp",EDGE,"E5.1.0")])],"isStart":true})});
            var Q13;
            Q13=makeQuery(id+"F2.boolean.opBoolean","COPY",EDGE,{"derivedFrom":makeQuery(id+"F2.opExtrude","CAP_EDGE",EDGE,{"disambiguationData":[OSD([sQuery(id+"F0.wireOp",EDGE,"E5.1.0")])],"isStart":false})});
            var Q14;
            Q14=makeQuery(id+"F2.boolean.opBoolean","COPY",EDGE,{"derivedFrom":makeQuery(id+"F2.opExtrude","CAP_EDGE",EDGE,{"disambiguationData":[OSD([sQuery(id+"F0.wireOp",EDGE,"E5.2.0")])],"isStart":true})});
            var Q15;
            Q15=makeQuery(id+"F2.boolean.opBoolean","COPY",EDGE,{"derivedFrom":makeQuery(id+"F2.opExtrude","CAP_EDGE",EDGE,{"disambiguationData":[OSD([sQuery(id+"F0.wireOp",EDGE,"E5.2.0")])],"isStart":false})});
            fillet(context, id + "F3", {"entities" : qUnion([Q0, Q1, Q2, Q3, Q4, Q5, Q6, Q7, Q8, Q9, Q10, Q11, Q12, Q13, Q14, Q15]), "radius" : 2 * mm, "tangentPropagation" : true, "allowEdgeOverflow" : false});
        }
    });
